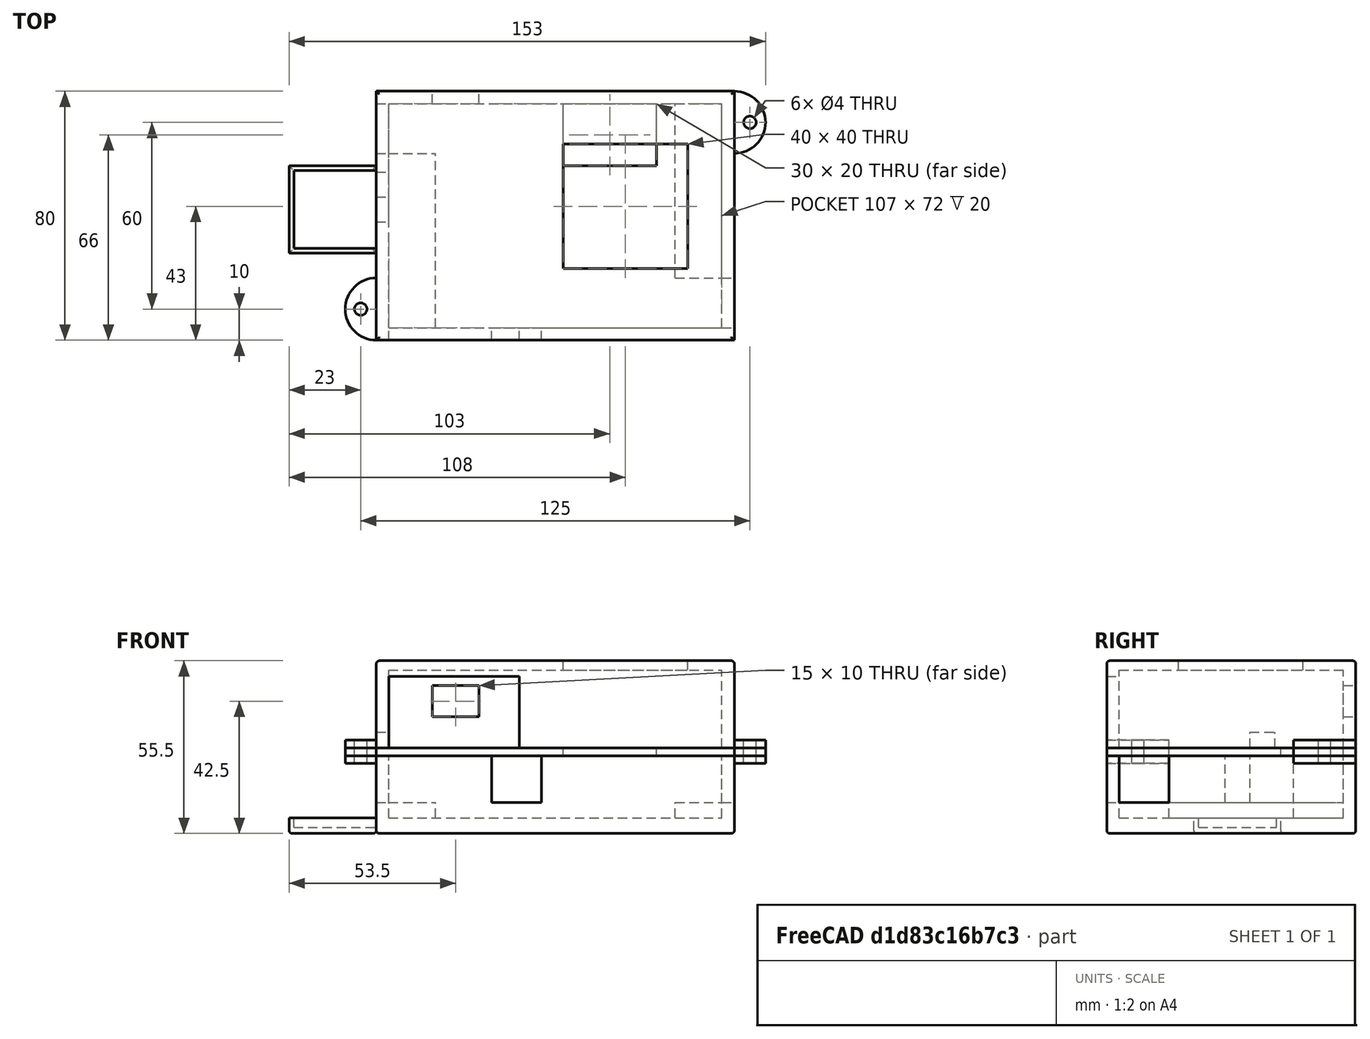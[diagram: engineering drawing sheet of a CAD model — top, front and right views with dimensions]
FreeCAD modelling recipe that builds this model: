
FCSTD DOCUMENT  (FreeCAD 0.18R4 (GitTag))
Label: Case
License: All rights reserved
LicenseURL: http://en.wikipedia.org/wiki/All_rights_reserved
objects: Part::Box×24, Part::Cut×24, Part::Cylinder×12, Part::Compound×3, Part::Fillet×3
note: 66 computed .brp shape members not serialized (recipe doc carries the construction recipe); baked Part::Feature solids carry a one-line shape summary decoded from their .brp

FEATURE [Part::Box] Box  label="Basis"
  AttacherType = Attacher::AttachEngine3D
  Height = 25
  Length = 115
  Width = 80
FEATURE [Part::Box] Box001  label="Basis_cut"
  AttacherType = Attacher::AttachEngine3D
  Height = 20
  Length = 107
  Placement = pos=(4,4,5) rot=(0,0,1;0rad)
  Width = 72
FEATURE [Part::Box] Box002  label="Solar"
  AttacherType = Attacher::AttachEngine3D
  Height = 15
  Length = 4
  Placement = pos=(0,60,10) rot=(0,0,1;0rad)
  Width = 16
FEATURE [Part::Box] Box003  label="Antenna"
  AttacherType = Attacher::AttachEngine3D
  Height = 15
  Length = 4
  Placement = pos=(111,4,10) rot=(0,0,1;0rad)
  Width = 16
FEATURE [Part::Box] Box004  label="Luftsensor"
  AttacherType = Attacher::AttachEngine3D
  Height = 15
  Length = 16
  Placement = pos=(37,0,10) rot=(0,0,1;0rad)
  Width = 4
FEATURE [Part::Box] Box005  label="Gps"
  AttacherType = Attacher::AttachEngine3D
  Height = 15
  Length = 4
  Placement = pos=(0,38,10) rot=(0,0,1;0rad)
  Width = 8
FEATURE [Part::Box] Box006  label="Holder"
  AttacherType = Attacher::AttachEngine3D
  Height = 5
  Length = 15
  Placement = pos=(4,4,5) rot=(0,0,1;0rad)
  Width = 56
FEATURE [Part::Box] Box007  label="Holder2"
  AttacherType = Attacher::AttachEngine3D
  Height = 5
  Length = 15
  Placement = pos=(96,20,5) rot=(0,0,1;0rad)
  Width = 56
FEATURE [Part::Cylinder] Cylinder  label="Cilindro"
  Angle = 360
  AttacherType = Attacher::AttachEngine3D
  Height = 2.5
  Placement = pos=(0,10,25) rot=(0,0,1;0rad)
  Radius = 10
FEATURE [Part::Cylinder] Cylinder001  label="Cilindro001"
  Angle = 360
  AttacherType = Attacher::AttachEngine3D
  Height = 2.5
  Placement = pos=(-5,10,25) rot=(0,0,1;0rad)
  Radius = 2
FEATURE [Part::Box] Box008  label="Cubo"
  AttacherType = Attacher::AttachEngine3D
  Height = 2.5
  Length = 10
  Placement = pos=(0,0,25) rot=(0,0,1;0rad)
  Width = 20
FEATURE [Part::Cut] Cut005
  Base = -> Cylinder
  Tool = -> Cylinder001
FEATURE [Part::Cut] Cut006
  Base = -> Cut005
  Placement = pos=(0,0,-2.5) rot=(0,0,1;0rad)
  Tool = -> Box008
FEATURE [Part::Box] Box009  label="Cubo001"
  AttacherType = Attacher::AttachEngine3D
  Height = 2.5
  Length = 10
  Placement = pos=(0,0,25) rot=(0,0,1;0rad)
  Width = 20
FEATURE [Part::Cylinder] Cylinder002  label="Cilindro002"
  Angle = 360
  AttacherType = Attacher::AttachEngine3D
  Height = 2.5
  Placement = pos=(-5,10,25) rot=(0,0,1;0rad)
  Radius = 2
FEATURE [Part::Cylinder] Cylinder003  label="Cilindro003"
  Angle = 360
  AttacherType = Attacher::AttachEngine3D
  Height = 2.5
  Placement = pos=(0,10,25) rot=(0,0,1;0rad)
  Radius = 10
FEATURE [Part::Cut] Cut007
  Base = -> Cylinder003
  Tool = -> Cylinder002
FEATURE [Part::Cut] Cut008
  Base = -> Cut007
  Placement = pos=(115,80,-2.5) rot=(0,0,1;3.14159rad)
  Tool = -> Box009
FEATURE [Part::Box] Box010  label="Cubo002"
  AttacherType = Attacher::AttachEngine3D
  Height = 2.5
  Length = 10
  Placement = pos=(0,0,25) rot=(0,0,1;0rad)
  Width = 20
FEATURE [Part::Cylinder] Cylinder004  label="Cilindro004"
  Angle = 360
  AttacherType = Attacher::AttachEngine3D
  Height = 2.5
  Placement = pos=(-5,10,25) rot=(0,0,1;0rad)
  Radius = 2
FEATURE [Part::Cylinder] Cylinder005  label="Cilindro005"
  Angle = 360
  AttacherType = Attacher::AttachEngine3D
  Height = 2.5
  Placement = pos=(0,10,25) rot=(0,0,1;0rad)
  Radius = 10
FEATURE [Part::Cut] Cut009
  Base = -> Cylinder005
  Tool = -> Cylinder004
FEATURE [Part::Cut] Cut010
  Base = -> Cut009
  Tool = -> Box010
FEATURE [Part::Box] Box011  label="Cubo003"
  AttacherType = Attacher::AttachEngine3D
  Height = 5
  Length = 10
  Placement = pos=(0,0,25) rot=(0,0,1;0rad)
  Width = 20
FEATURE [Part::Cylinder] Cylinder006  label="Cilindro006"
  Angle = 360
  AttacherType = Attacher::AttachEngine3D
  Height = 2.5
  Placement = pos=(0,10,25) rot=(0,0,1;0rad)
  Radius = 10
FEATURE [Part::Cylinder] Cylinder007  label="Cilindro007"
  Angle = 360
  AttacherType = Attacher::AttachEngine3D
  Height = 2.5
  Placement = pos=(-5,10,25) rot=(0,0,1;0rad)
  Radius = 2
FEATURE [Part::Cut] Cut011
  Base = -> Cylinder006
  Tool = -> Cylinder007
FEATURE [Part::Cut] Cut012
  Base = -> Cut011
  Placement = pos=(115,80,0) rot=(0,0,1;3.14159rad)
  Tool = -> Box011
FEATURE [Part::Box] Box012  label="Cubo004"
  AttacherType = Attacher::AttachEngine3D
  Height = 2.5
  Length = 115
  Placement = pos=(0,0,25) rot=(0,0,1;0rad)
  Width = 80
FEATURE [Part::Cut] Cut
  Base = -> Box
  Tool = -> Box001
FEATURE [Part::Cut] Cut013
  Base = -> Cut
  Tool = -> Box002
FEATURE [Part::Cut] Cut014
  Base = -> Cut013
  Tool = -> Box003
FEATURE [Part::Cut] Cut015
  Base = -> Cut014
  Tool = -> Box004
FEATURE [Part::Cut] Cut016
  Base = -> Cut015
  Tool = -> Box005
FEATURE [Part::Box] Box013  label="Cubo005"
  AttacherType = Attacher::AttachEngine3D
  Height = 2.5
  Length = 30
  Placement = pos=(60,56,25) rot=(0,0,1;0rad)
  Width = 20
FEATURE [Part::Cut] Cut017
  Base = -> Box012
  Tool = -> Box013
FEATURE [Part::Compound] Compound001  label="Mitte"
  Links = -> [Cut017,Cut012,Cut010]
FEATURE [Part::Box] Box014  label="Cubo006"
  AttacherType = Attacher::AttachEngine3D
  Height = 5
  Length = 28
  Placement = pos=(-28,28,0) rot=(0,0,1;0rad)
  Width = 28
FEATURE [Part::Box] Box015  label="Cubo007"
  AttacherType = Attacher::AttachEngine3D
  Height = 3
  Length = 26.5
  Placement = pos=(-26.5,29.5,2) rot=(0,0,1;0rad)
  Width = 25
FEATURE [Part::Cut] Cut018
  Base = -> Box014
  Tool = -> Box015
FEATURE [Part::Compound] Compound  label="Base"
  Links = -> [Cut016,Cut008,Cut006,Box007,Box006,Cut018]
FEATURE [Part::Cylinder] Cylinder008  label="Cilindro008"
  Angle = 360
  AttacherType = Attacher::AttachEngine3D
  Height = 2.5
  Placement = pos=(0,10,25) rot=(0,0,1;0rad)
  Radius = 10
FEATURE [Part::Cylinder] Cylinder009  label="Cilindro009"
  Angle = 360
  AttacherType = Attacher::AttachEngine3D
  Height = 2.5
  Placement = pos=(-5,10,25) rot=(0,0,1;0rad)
  Radius = 2
FEATURE [Part::Cut] Cut019
  Base = -> Cylinder008
  Tool = -> Cylinder009
FEATURE [Part::Box] Box016  label="Cubo008"
  AttacherType = Attacher::AttachEngine3D
  Height = 5
  Length = 10
  Placement = pos=(0,0,25) rot=(0,0,1;0rad)
  Width = 20
FEATURE [Part::Cut] Cut020
  Base = -> Cut019
  Placement = pos=(115,80,2.5) rot=(0,0,1;3.14159rad)
  Tool = -> Box016
FEATURE [Part::Box] Box017  label="Cubo009"
  AttacherType = Attacher::AttachEngine3D
  Height = 2.5
  Length = 10
  Placement = pos=(0,0,25) rot=(0,0,1;0rad)
  Width = 20
FEATURE [Part::Cylinder] Cylinder010  label="Cilindro010"
  Angle = 360
  AttacherType = Attacher::AttachEngine3D
  Height = 2.5
  Placement = pos=(0,10,25) rot=(0,0,1;0rad)
  Radius = 10
FEATURE [Part::Cylinder] Cylinder011  label="Cilindro011"
  Angle = 360
  AttacherType = Attacher::AttachEngine3D
  Height = 2.5
  Placement = pos=(-5,10,25) rot=(0,0,1;0rad)
  Radius = 2
FEATURE [Part::Cut] Cut022
  Base = -> Cylinder010
  Tool = -> Cylinder011
FEATURE [Part::Cut] Cut021
  Base = -> Cut022
  Placement = pos=(0,0,2.5) rot=(0,0,1;0rad)
  Tool = -> Box017
FEATURE [Part::Box] Box018  label="Cubo010"
  AttacherType = Attacher::AttachEngine3D
  Height = 28
  Length = 115
  Placement = pos=(0,0,27.5) rot=(0,0,1;0rad)
  Width = 80
FEATURE [Part::Box] Box019  label="Cubo011"
  AttacherType = Attacher::AttachEngine3D
  Height = 25
  Length = 107
  Placement = pos=(4,4,27.5) rot=(0,0,1;0rad)
  Width = 72
FEATURE [Part::Box] Box020  label="Cubo012"
  AttacherType = Attacher::AttachEngine3D
  Height = 23
  Length = 42
  Placement = pos=(4,0,27.5) rot=(0,0,1;0rad)
  Width = 4
FEATURE [Part::Box] Box021  label="Cubo013"
  AttacherType = Attacher::AttachEngine3D
  Height = 10
  Length = 15
  Placement = pos=(18,76,37.5) rot=(0,0,1;0rad)
  Width = 4
FEATURE [Part::Cut] Cut023
  Base = -> Box018
  Tool = -> Box019
FEATURE [Part::Cut] Cut024
  Base = -> Cut023
  Tool = -> Box020
FEATURE [Part::Cut] Cut025
  Base = -> Cut024
  Tool = -> Box021
FEATURE [Part::Box] Box022  label="Cubo014"
  AttacherType = Attacher::AttachEngine3D
  Height = 3
  Length = 40
  Placement = pos=(60,23,52.5) rot=(0,0,1;0rad)
  Width = 40
FEATURE [Part::Cut] Cut026
  Base = -> Cut025
  Tool = -> Box022
FEATURE [Part::Box] Box023  label="Cubo015"
  AttacherType = Attacher::AttachEngine3D
  Height = 5
  Length = 4
  Placement = pos=(0,46,27.5) rot=(0,0,1;0rad)
  Width = 8
FEATURE [Part::Cut] Cut027
  Base = -> Cut026
  Tool = -> Box023
FEATURE [Part::Compound] Compound002  label="Top"
  Links = -> [Cut020,Cut021,Cut027]
FEATURE [Part::Fillet] Fillet  label="Top003"
  Base = -> Compound002
  Edges = 4 edges r=1: [Edge19,Edge27,Edge28,Edge29]
FEATURE [Part::Fillet] Fillet001
  Base = -> Compound
  Edges = 4 edges r=1: [Edge11,Edge37,Edge39,Edge40]
FEATURE [Part::Fillet] Fillet002  label="Base001"
  Base = -> Fillet001
  Edges = 4 edges r=1: [Edge124,Edge125,Edge134,Edge136]
